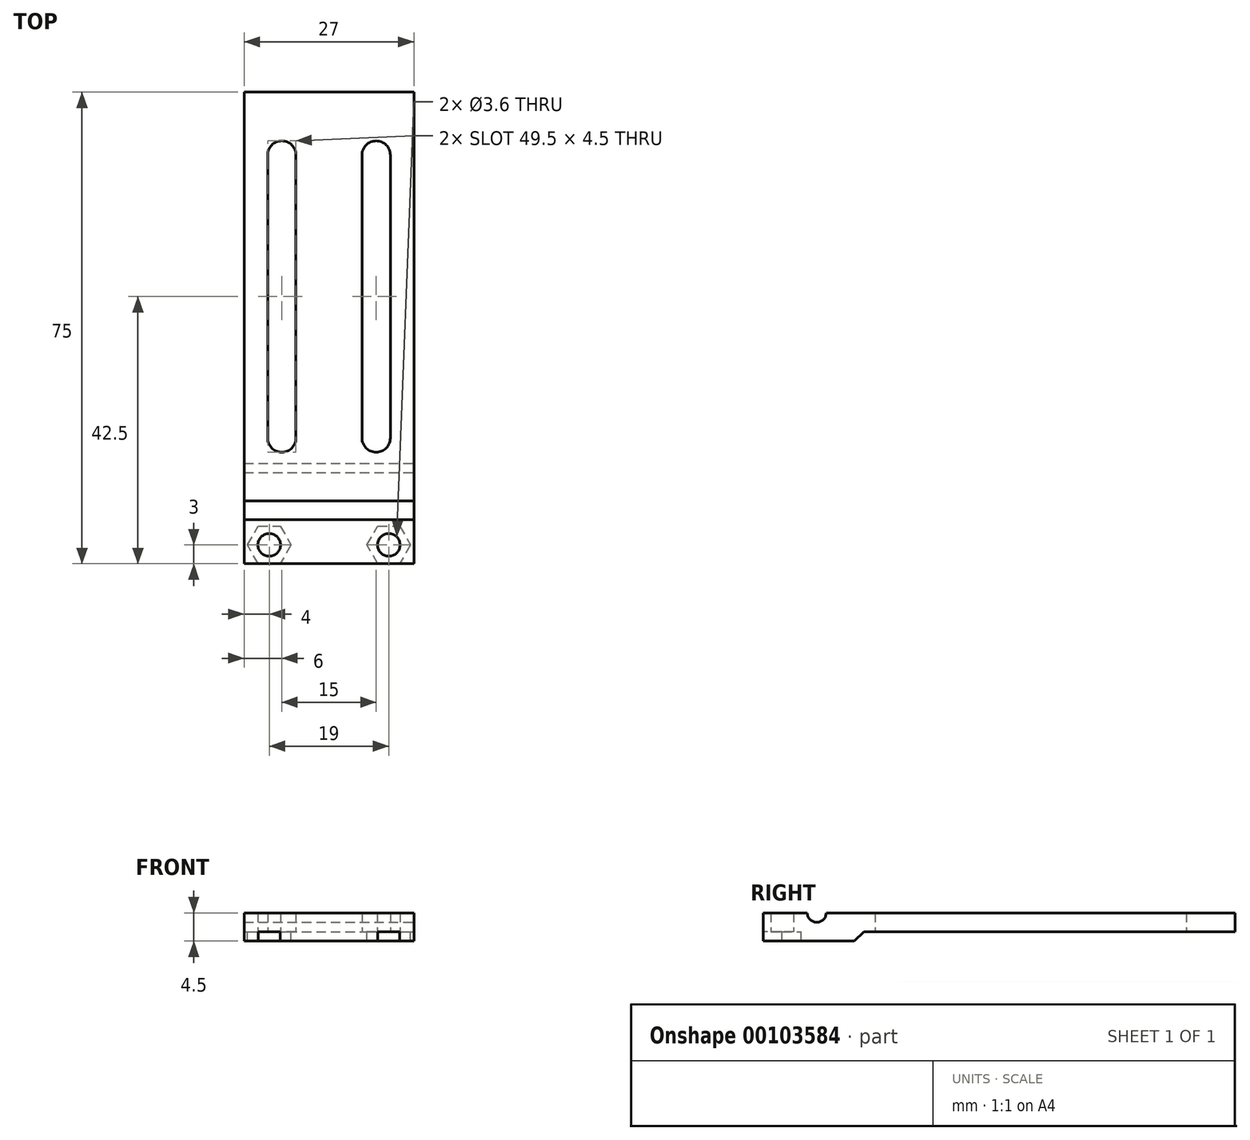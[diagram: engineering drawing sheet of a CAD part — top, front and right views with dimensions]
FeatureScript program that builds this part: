
annotation { "Feature Type Name" : "Feature", "Feature Type Description" : "" }
export const myFeature = defineFeature(function(context is Context, id is Id, definition is map)
    precondition{}
    {
        {
            var Q0;
            Q0=qCreatedBy(makeId("Top.planeOp"),FACE);
            var sketch = newSketch(context, id + "F0", { "sketchPlane" : qUnion([Q0])});
            skLineSegment(sketch, "E0.bottom", {"start": v(0, 0) * mm, "end": v(27, 0) * mm});
            skLineSegment(sketch, "E0.top", {"start": v(0, -75) * mm, "end": v(27, -75) * mm});
            skLineSegment(sketch, "E0.left", {"start": v(0, 0) * mm, "end": v(0, -75) * mm});
            skLineSegment(sketch, "E0.right", {"start": v(27, 0) * mm, "end": v(27, -75) * mm});
            skCircle(sketch, "E1", {"center": v(4, -72) * mm, "radius": 1.8 * mm});
            skCircle(sketch, "E2", {"center": v(23, -72) * mm, "radius": 1.8 * mm});
            skCircle(sketch, "E3", {"center": v(6, -10) * mm, "radius": 2.25 * mm, "construction": true});
            skCircle(sketch, "E4", {"center": v(21, -10) * mm, "radius": 2.25 * mm, "construction": true});
            skCircle(sketch, "E5", {"center": v(6, -55) * mm, "radius": 2.25 * mm, "construction": true});
            skCircle(sketch, "E6", {"center": v(21, -55) * mm, "radius": 2.25 * mm, "construction": true});
            skLineSegment(sketch, "E7", {"start": v(3.75, -10) * mm, "end": v(3.75, -55) * mm});
            skLineSegment(sketch, "E8", {"start": v(8.25, -10) * mm, "end": v(8.25, -55) * mm});
            skLineSegment(sketch, "E9", {"start": v(18.75, -10) * mm, "end": v(18.75, -55) * mm});
            skLineSegment(sketch, "E10", {"start": v(23.25, -10) * mm, "end": v(23.25, -55) * mm});
            skArc(sketch, "E11", {"start": v(3.75, -10) * mm, "mid": v(6, -7.75) * mm, "end": v(8.25, -10) * mm});
            skArc(sketch, "E12", {"start": v(18.75, -10) * mm, "mid": v(21, -7.75) * mm, "end": v(23.25, -10) * mm});
            skArc(sketch, "E13", {"start": v(23.25, -55) * mm, "mid": v(21, -57.25) * mm, "end": v(18.75, -55) * mm});
            skArc(sketch, "E14", {"start": v(8.25, -55) * mm, "mid": v(6, -57.25) * mm, "end": v(3.75, -55) * mm});
            skCircle(sketch, "E15.cCircle", {"center": v(4, -72) * mm, "radius": 3 * mm, "construction": true});
            skLineSegment(sketch, "E15.0", {"start": v(2.27, -69) * mm, "end": v(5.73, -69) * mm});
            skLineSegment(sketch, "E15.1", {"start": v(5.73, -69) * mm, "end": v(7.46, -72) * mm});
            skLineSegment(sketch, "E15.2", {"start": v(7.46, -72) * mm, "end": v(5.73, -75) * mm});
            skLineSegment(sketch, "E15.3", {"start": v(5.73, -75) * mm, "end": v(2.27, -75) * mm});
            skLineSegment(sketch, "E15.4", {"start": v(2.27, -75) * mm, "end": v(0.54, -72) * mm});
            skLineSegment(sketch, "E15.5", {"start": v(0.54, -72) * mm, "end": v(2.27, -69) * mm});
            skPoint(sketch, "E15.0.midPoint", {"position": v(4, -69) * mm});
            skCircle(sketch, "E16.cCircle", {"center": v(23, -72) * mm, "radius": 3 * mm, "construction": true});
            skLineSegment(sketch, "E16.0", {"start": v(21.27, -69) * mm, "end": v(24.73, -69) * mm});
            skLineSegment(sketch, "E16.1", {"start": v(24.73, -69) * mm, "end": v(26.46, -72) * mm});
            skLineSegment(sketch, "E16.2", {"start": v(26.46, -72) * mm, "end": v(24.73, -75) * mm});
            skLineSegment(sketch, "E16.3", {"start": v(24.73, -75) * mm, "end": v(21.27, -75) * mm});
            skLineSegment(sketch, "E16.4", {"start": v(21.27, -75) * mm, "end": v(19.54, -72) * mm});
            skLineSegment(sketch, "E16.5", {"start": v(19.54, -72) * mm, "end": v(21.27, -69) * mm});
            skPoint(sketch, "E16.0.midPoint", {"position": v(23, -69) * mm});
            skSolve(sketch);
        }
        {
            var Q0;
            Q0=makeQuery(id+"F0.imprint","IMPRINT",FACE,{"disambiguationData":[TD([[makeQuery(id+"F0.imprint","IMPRINT",EDGE,{"derivedFrom":sQuery(id+"F0.wireOp",EDGE,"E0.bottom")}),-1.0]])]});
            var Q1;
            Q1=makeQuery(id+"F0.imprint","IMPRINT",FACE,{"disambiguationData":[TD([[makeQuery(id+"F0.imprint","IMPRINT",EDGE,{"derivedFrom":sQuery(id+"F0.wireOp",EDGE,"E2")}),-1.0]])]});
            var Q2;
            Q2=makeQuery(id+"F0.imprint","IMPRINT",FACE,{"disambiguationData":[TD([[makeQuery(id+"F0.imprint","IMPRINT",EDGE,{"derivedFrom":sQuery(id+"F0.wireOp",EDGE,"E1")}),-1.0]])]});
            extrude(context, id + "F1", {"entities" : qUnion([Q0, Q1, Q2]), "depth" : 3 * mm});
        }
        {
            var Q0;
            Q0=makeQuery(id+"F1.opExtrude","SWEPT_FACE",FACE,{"disambiguationData":[OSD([sQuery(id+"F0.wireOp",EDGE,"E0.right")])]});
            var sketch = newSketch(context, id + "F2", { "sketchPlane" : qUnion([Q0])});
            skPoint(sketch, "E17.0", {"position": v(-72, 0) * mm});
            skLineSegment(sketch, "E18", {"start": v(-72, 0) * mm, "end": v(-72, 3) * mm, "construction": true});
            skArc(sketch, "E19", {"start": v(-68, 3) * mm, "mid": v(-66.5, 1.5) * mm, "end": v(-65, 3) * mm});
            skLineSegment(sketch, "E20", {"start": v(-75, 0) * mm, "end": v(-75, -1.5) * mm});
            skLineSegment(sketch, "E21", {"start": v(-75, -1.5) * mm, "end": v(-60.5, -1.5) * mm});
            skLineSegment(sketch, "E22", {"start": v(-60.5, -1.5) * mm, "end": v(-59, 0) * mm});
            skSolve(sketch);
        }
        {
            var Q0;
            Q0 = qSketchRegion(id + "F2", true);
            var Q1;
            {var subQ0=sQuery(id+"F2.wireOp",EDGE,"E19");Q1=makeQuery(id+"F2.imprint","IMPRINT",FACE,{"disambiguationData":[TD([[makeQuery(id+"F2.imprint","IMPRINT",EDGE,{"derivedFrom":subQ0}),1.0]])]});}
            extrude(context, id + "F3", {"entities" : qUnion([Q0, Q1]), "operationType" : NewBodyOperationType.REMOVE, "endBound" : BoundingType.UP_TO_NEXT, "oppositeDirection" : true, "depth" : 25 * mm});
        }
        {
            var Q0;
            {var subQ0=sQuery(id+"F2.wireOp",EDGE,"E20");Q0=makeQuery(id+"F2.imprint","IMPRINT",FACE,{"disambiguationData":[TD([[makeQuery(id+"F2.imprint","IMPRINT",EDGE,{"derivedFrom":subQ0}),1.0]])]});}
            var Q1;
            Q1=makeQuery(id+"F1.opExtrude","SWEPT_FACE",FACE,{"disambiguationData":[OSD([sQuery(id+"F0.wireOp",EDGE,"E0.left")])]});
            extrude(context, id + "F4", {"entities" : qUnion([Q0]), "operationType" : NewBodyOperationType.ADD, "endBound" : BoundingType.UP_TO_SURFACE, "oppositeDirection" : true, "endBoundEntityFace" : qUnion([Q1]), "depth" : 25 * mm});
        }
        {
            var Q0;
            Q0=makeQuery(id+"F0.imprint","IMPRINT",FACE,{"disambiguationData":[TD([[makeQuery(id+"F0.imprint","IMPRINT",EDGE,{"derivedFrom":sQuery(id+"F0.wireOp",EDGE,"E1")}),1.0]])]});
            var Q1;
            Q1=makeQuery(id+"F0.imprint","IMPRINT",FACE,{"disambiguationData":[TD([[makeQuery(id+"F0.imprint","IMPRINT",EDGE,{"derivedFrom":sQuery(id+"F0.wireOp",EDGE,"E2")}),1.0]])]});
            var Q2;
            Q2=makeQuery(id+"F0.imprint","IMPRINT",FACE,{"disambiguationData":[TD([[makeQuery(id+"F0.imprint","IMPRINT",EDGE,{"derivedFrom":sQuery(id+"F0.wireOp",EDGE,"E1")}),-1.0]])]});
            var Q3;
            Q3=makeQuery(id+"F0.imprint","IMPRINT",FACE,{"disambiguationData":[TD([[makeQuery(id+"F0.imprint","IMPRINT",EDGE,{"derivedFrom":sQuery(id+"F0.wireOp",EDGE,"E2")}),-1.0]])]});
            extrude(context, id + "F5", {"entities" : qUnion([Q0, Q1, Q2, Q3]), "operationType" : NewBodyOperationType.REMOVE, "endBound" : BoundingType.UP_TO_NEXT, "oppositeDirection" : true, "depth" : 25 * mm});
        }
    });
